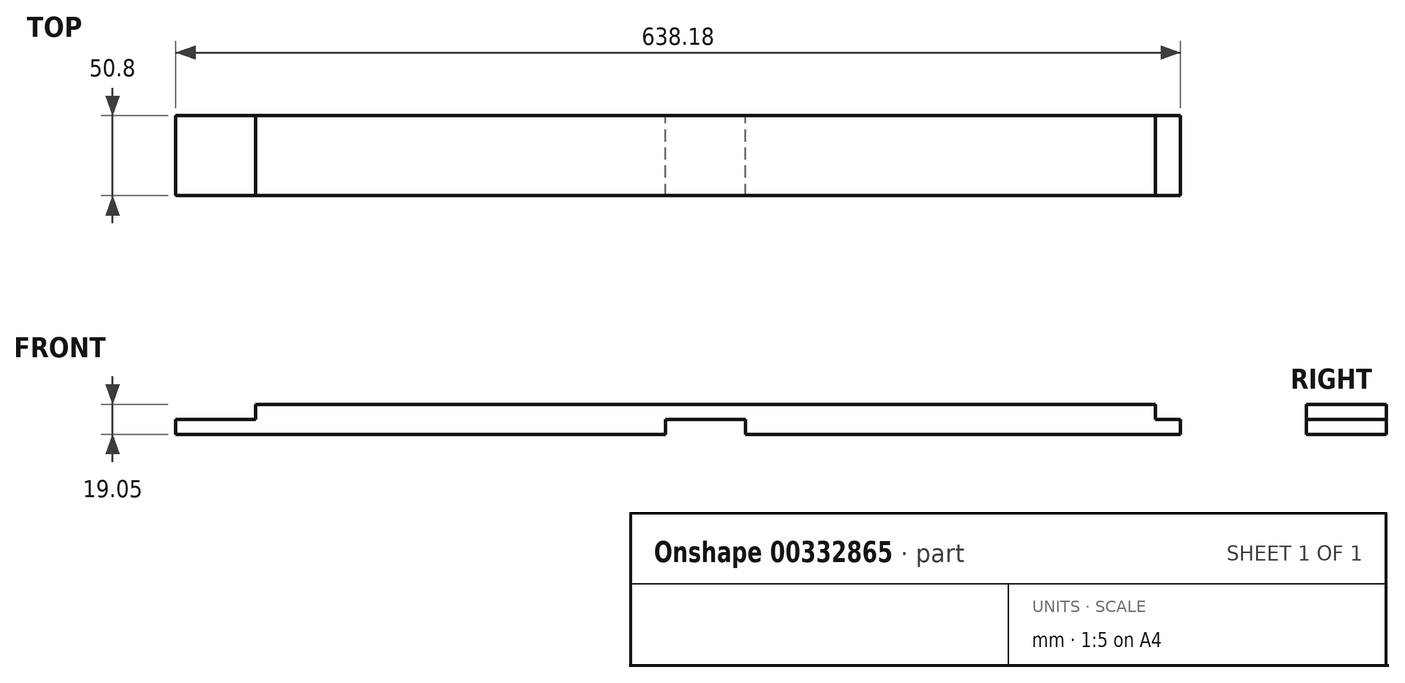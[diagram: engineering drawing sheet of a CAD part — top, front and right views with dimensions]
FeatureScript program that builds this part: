
annotation { "Feature Type Name" : "Feature", "Feature Type Description" : "" }
export const myFeature = defineFeature(function(context is Context, id is Id, definition is map)
    precondition{}
    {
        {
            var Q0;
            Q0=qCreatedBy(makeId("Front.planeOp"),FACE);
            var sketch = newSketch(context, id + "F0", { "sketchPlane" : qUnion([Q0])});
            skLineSegment(sketch, "E0", {"start": v(1612.5, -19.05) * mm, "end": v(1336.28, -19.05) * mm});
            skPoint(sketch, "E1.left.start.orphan", {"position": v(-798.41, -3.82) * mm});
            skLineSegment(sketch, "E2.left", {"start": v(1596.63, -9.53) * mm, "end": v(1596.63, 0) * mm});
            skLineSegment(sketch, "E3.top", {"start": v(1596.63, -9.53) * mm, "end": v(1612.5, -9.53) * mm});
            skPoint(sketch, "E4.orphan", {"position": v(1631.95, -33.78) * mm});
            skLineSegment(sketch, "E5", {"start": v(1612.5, -9.53) * mm, "end": v(1612.5, -19.05) * mm});
            skLineSegment(sketch, "E6", {"start": v(974.33, -9.53) * mm, "end": v(974.33, -19.05) * mm});
            skLineSegment(sketch, "E7.trimOffspring", {"start": v(1025.13, 0) * mm, "end": v(1596.63, 0) * mm});
            skPoint(sketch, "E8.start.orphan", {"position": v(0, 0) * mm});
            skLineSegment(sketch, "E9.bottom", {"start": v(974.33, -9.53) * mm, "end": v(1025.13, -9.53) * mm});
            skLineSegment(sketch, "E9.right", {"start": v(1025.13, -9.53) * mm, "end": v(1025.13, 0) * mm});
            skLineSegment(sketch, "E10", {"start": v(1310.88, 0) * mm, "end": v(1310.88, -190.58) * mm, "construction": true});
            skLineSegment(sketch, "E11.bottom", {"start": v(1336.28, -9.53) * mm, "end": v(1285.48, -9.53) * mm});
            skLineSegment(sketch, "E11.left", {"start": v(1336.28, -9.53) * mm, "end": v(1336.28, -19.05) * mm});
            skLineSegment(sketch, "E11.right", {"start": v(1285.48, -9.53) * mm, "end": v(1285.48, -19.05) * mm});
            skPoint(sketch, "E11.middle", {"position": v(1310.88, -19.05) * mm});
            skLineSegment(sketch, "E12.trimOffspring", {"start": v(1285.48, -19.05) * mm, "end": v(974.33, -19.05) * mm});
            skPoint(sketch, "E13.orphan", {"position": v(1336.28, -28.57) * mm});
            skPoint(sketch, "E14.orphan", {"position": v(1285.48, -28.58) * mm});
            skSolve(sketch);
        }
        {
            var Q0;
            Q0=qSketchRegion(id+"F0",true);
            extrude(context, id + "F1", {"entities" : qUnion([Q0]), "depth" : 50.8 * mm});
        }
    });
